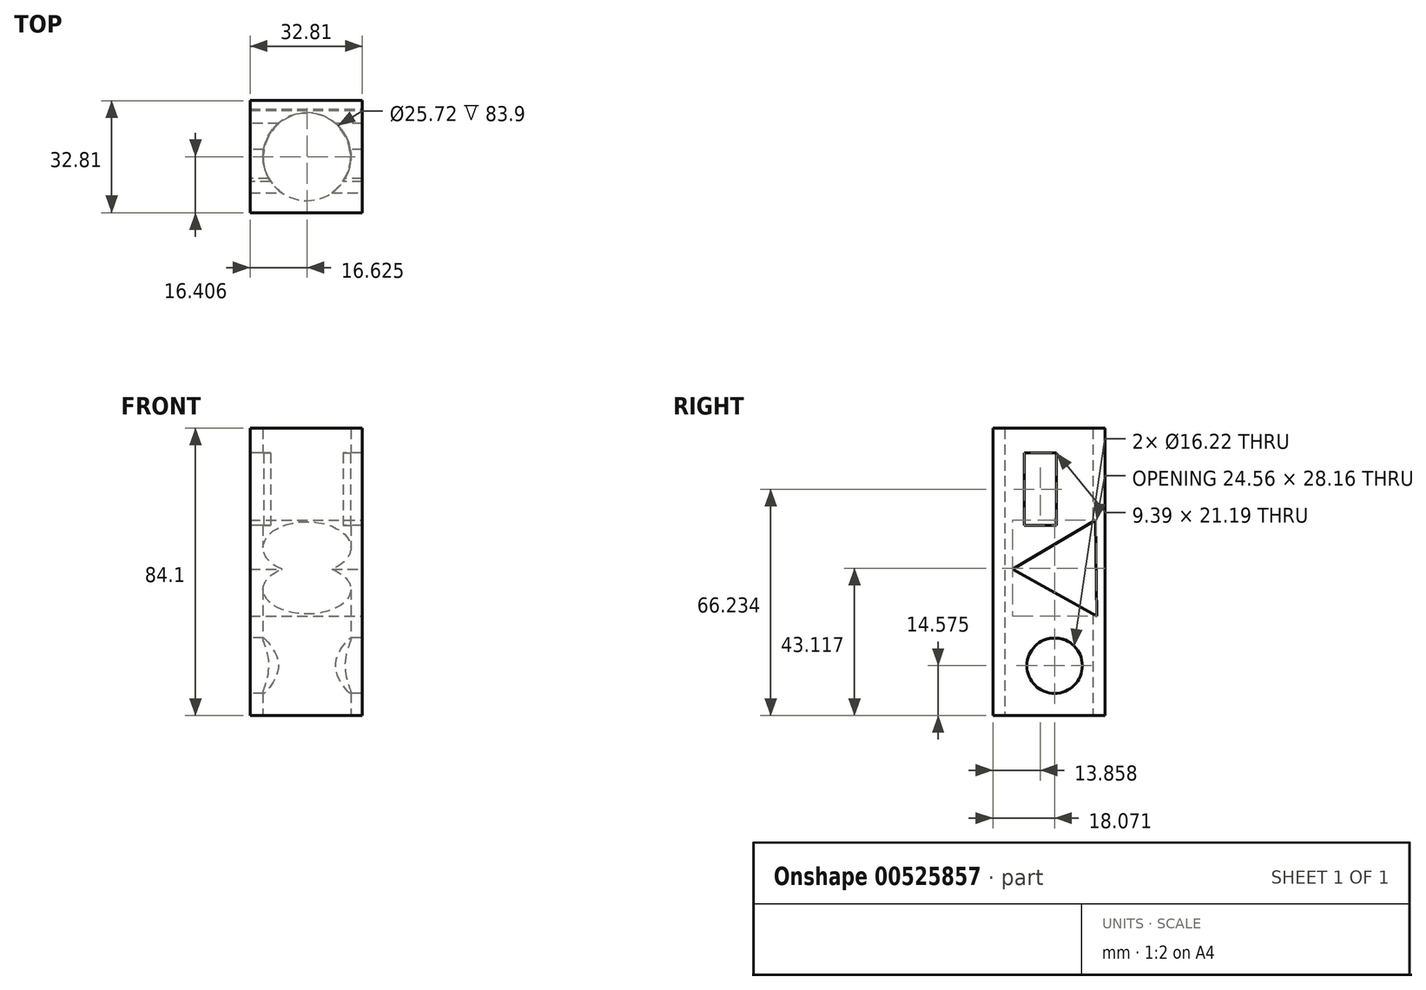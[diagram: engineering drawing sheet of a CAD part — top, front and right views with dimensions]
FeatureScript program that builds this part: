
annotation { "Feature Type Name" : "Feature", "Feature Type Description" : "" }
export const myFeature = defineFeature(function(context is Context, id is Id, definition is map)
    precondition{}
    {
        {
            var Q0;
            Q0=qCreatedBy(makeId("Top.planeOp"),FACE);
            var sketch = newSketch(context, id + "F0", { "sketchPlane" : qUnion([Q0])});
            skLineSegment(sketch, "E0.bottom", {"start": v(0, 32.81) * mm, "end": v(32.81, 32.81) * mm});
            skLineSegment(sketch, "E0.top", {"start": v(0, 0) * mm, "end": v(32.81, 0) * mm});
            skLineSegment(sketch, "E0.left", {"start": v(0, 32.81) * mm, "end": v(0, 0) * mm});
            skLineSegment(sketch, "E0.right", {"start": v(32.81, 32.81) * mm, "end": v(32.81, 0) * mm});
            skSolve(sketch);
        }
        {
            var Q0;
            Q0=makeQuery(id+"F0.imprint","IMPRINT",FACE,{"disambiguationData":[TD([[makeQuery(id+"F0.imprint","IMPRINT",EDGE,{"derivedFrom":sQuery(id+"F0.wireOp",EDGE,"E0.bottom")}),-1.0]])]});
            extrude(context, id + "F1", {"entities" : qUnion([Q0]), "depth" : 84.1 * mm, "offsetDistance" : 25 * mm});
        }
        {
            var Q0;
            Q0=qCreatedBy(makeId("Front.planeOp"),FACE);
            var sketch = newSketch(context, id + "F2", { "sketchPlane" : qUnion([Q0])});
            skCircle(sketch, "E1", {"center": v(-41.37, 38.64) * mm, "radius": 18.06 * mm});
            skSolve(sketch);
        }
        {
            var Q0;
            Q0=makeQuery(id+"F2.imprint","IMPRINT",FACE,{"disambiguationData":[TD([[makeQuery(id+"F2.imprint","IMPRINT",EDGE,{"derivedFrom":sQuery(id+"F2.wireOp",EDGE,"E1")}),1.0]])]});
            extrude(context, id + "F3", {"entities" : qUnion([Q0]), "operationType" : NewBodyOperationType.REMOVE, "oppositeDirection" : true, "depth" : 25 * mm, "offsetDistance" : 25 * mm});
        }
        {
            var Q0;
            Q0=makeQuery(id+"F1.opExtrude","CAP_FACE",FACE,{"disambiguationData":[OSD([sQuery(id+"F0.wireOp",EDGE,"E0.bottom"),sQuery(id+"F0.wireOp",EDGE,"E0.top"),sQuery(id+"F0.wireOp",EDGE,"E0.left"),sQuery(id+"F0.wireOp",EDGE,"E0.right")])],"isStart":true});
            var sketch = newSketch(context, id + "F4", { "sketchPlane" : qUnion([Q0])});
            skCircle(sketch, "E2", {"center": v(16.63, -16.4) * mm, "radius": 12.86 * mm});
            skSolve(sketch);
        }
        {
            var Q0;
            Q0=makeQuery(id+"F4.imprint","IMPRINT",FACE,{"disambiguationData":[TD([[makeQuery(id+"F4.imprint","IMPRINT",EDGE,{"derivedFrom":sQuery(id+"F4.wireOp",EDGE,"E2")}),1.0]])]});
            extrude(context, id + "F5", {"entities" : qUnion([Q0]), "operationType" : NewBodyOperationType.REMOVE, "oppositeDirection" : true, "depth" : 83.9 * mm, "offsetDistance" : 25 * mm});
        }
        {
            var Q0;
            Q0=makeQuery(id+"F5.boolean.opBoolean","COPY",FACE,{"derivedFrom":makeQuery(id+"F5.opExtrude","CAP_FACE",FACE,{"disambiguationData":[OSD([sQuery(id+"F4.wireOp",EDGE,"E2")])],"isStart":false})});
            var sketch = newSketch(context, id + "F6", { "sketchPlane" : qUnion([Q0])});
            skCircle(sketch, "E3", {"center": v(16.63, -16.4) * mm, "radius": 12.58 * mm});
            skSolve(sketch);
        }
        {
            var Q0;
            Q0=makeQuery(id+"F6.imprint","IMPRINT",FACE,{"disambiguationData":[TD([[makeQuery(id+"F6.imprint","IMPRINT",EDGE,{"derivedFrom":sQuery(id+"F6.wireOp",EDGE,"E3")}),1.0]])]});
            extrude(context, id + "F7", {"entities" : qUnion([Q0]), "operationType" : NewBodyOperationType.REMOVE, "depth" : 95.8 * mm, "offsetDistance" : 25 * mm});
        }
        {
            var Q0;
            Q0=makeQuery(id+"F1.opExtrude","SWEPT_FACE",FACE,{"disambiguationData":[OSD([sQuery(id+"F0.wireOp",EDGE,"E0.right")])]});
            var sketch = newSketch(context, id + "F8", { "sketchPlane" : qUnion([Q0])});
            skCircle(sketch, "E4.cCircle", {"center": v(22.05, 43.02) * mm, "radius": 8.13 * mm, "construction": true});
            skLineSegment(sketch, "E4.0", {"start": v(5.8, 42.82) * mm, "end": v(30, 57.2) * mm});
            skLineSegment(sketch, "E4.1", {"start": v(30, 57.2) * mm, "end": v(30.35, 29.04) * mm});
            skLineSegment(sketch, "E4.2", {"start": v(30.35, 29.04) * mm, "end": v(5.8, 42.82) * mm});
            skPoint(sketch, "E4.0.midPoint", {"position": v(17.9, 50) * mm});
            skSolve(sketch);
        }
        {
            var Q0;
            Q0=makeQuery(id+"F8.imprint","IMPRINT",FACE,{"disambiguationData":[TD([[makeQuery(id+"F8.imprint","IMPRINT",EDGE,{"derivedFrom":sQuery(id+"F8.wireOp",EDGE,"E4.0")}),-1.0]])]});
            extrude(context, id + "F9", {"entities" : qUnion([Q0]), "operationType" : NewBodyOperationType.REMOVE, "oppositeDirection" : true, "depth" : 47.1 * mm, "offsetDistance" : 25 * mm});
        }
        {
            var Q0;
            Q0=makeQuery(id+"F1.opExtrude","SWEPT_FACE",FACE,{"disambiguationData":[OSD([sQuery(id+"F0.wireOp",EDGE,"E0.left")])]});
            var sketch = newSketch(context, id + "F10", { "sketchPlane" : qUnion([Q0])});
            skCircle(sketch, "E5", {"center": v(-18.07, 14.57) * mm, "radius": 8.11 * mm});
            skPoint(sketch, "E5.centerSnap0", {"position": v(-18.07, 35.93) * mm});
            skSolve(sketch);
        }
        {
            var Q0;
            Q0=makeQuery(id+"F10.imprint","IMPRINT",FACE,{"disambiguationData":[TD([[makeQuery(id+"F10.imprint","IMPRINT",EDGE,{"derivedFrom":sQuery(id+"F10.wireOp",EDGE,"E5")}),1.0]])]});
            extrude(context, id + "F11", {"entities" : qUnion([Q0]), "operationType" : NewBodyOperationType.REMOVE, "oppositeDirection" : true, "depth" : 55.8 * mm, "offsetDistance" : 25 * mm});
        }
        {
            var Q0;
            Q0=makeQuery(id+"F1.opExtrude","SWEPT_FACE",FACE,{"disambiguationData":[OSD([sQuery(id+"F0.wireOp",EDGE,"E0.left")])]});
            var sketch = newSketch(context, id + "F12", { "sketchPlane" : qUnion([Q0])});
            skLineSegment(sketch, "E6.bottom", {"start": v(-9.16, 76.83) * mm, "end": v(-18.55, 76.83) * mm});
            skLineSegment(sketch, "E6.top", {"start": v(-9.16, 55.64) * mm, "end": v(-18.55, 55.64) * mm});
            skLineSegment(sketch, "E6.left", {"start": v(-9.16, 76.83) * mm, "end": v(-9.16, 55.64) * mm});
            skLineSegment(sketch, "E6.right", {"start": v(-18.55, 76.83) * mm, "end": v(-18.55, 55.64) * mm});
            skSolve(sketch);
        }
        {
            var Q0;
            Q0=makeQuery(id+"F12.imprint","IMPRINT",FACE,{"disambiguationData":[TD([[makeQuery(id+"F12.imprint","IMPRINT",EDGE,{"derivedFrom":sQuery(id+"F12.wireOp",EDGE,"E6.bottom")}),1.0]])]});
            extrude(context, id + "F13", {"entities" : qUnion([Q0]), "operationType" : NewBodyOperationType.REMOVE, "oppositeDirection" : true, "depth" : 42.9 * mm, "offsetDistance" : 25 * mm});
        }
    });
